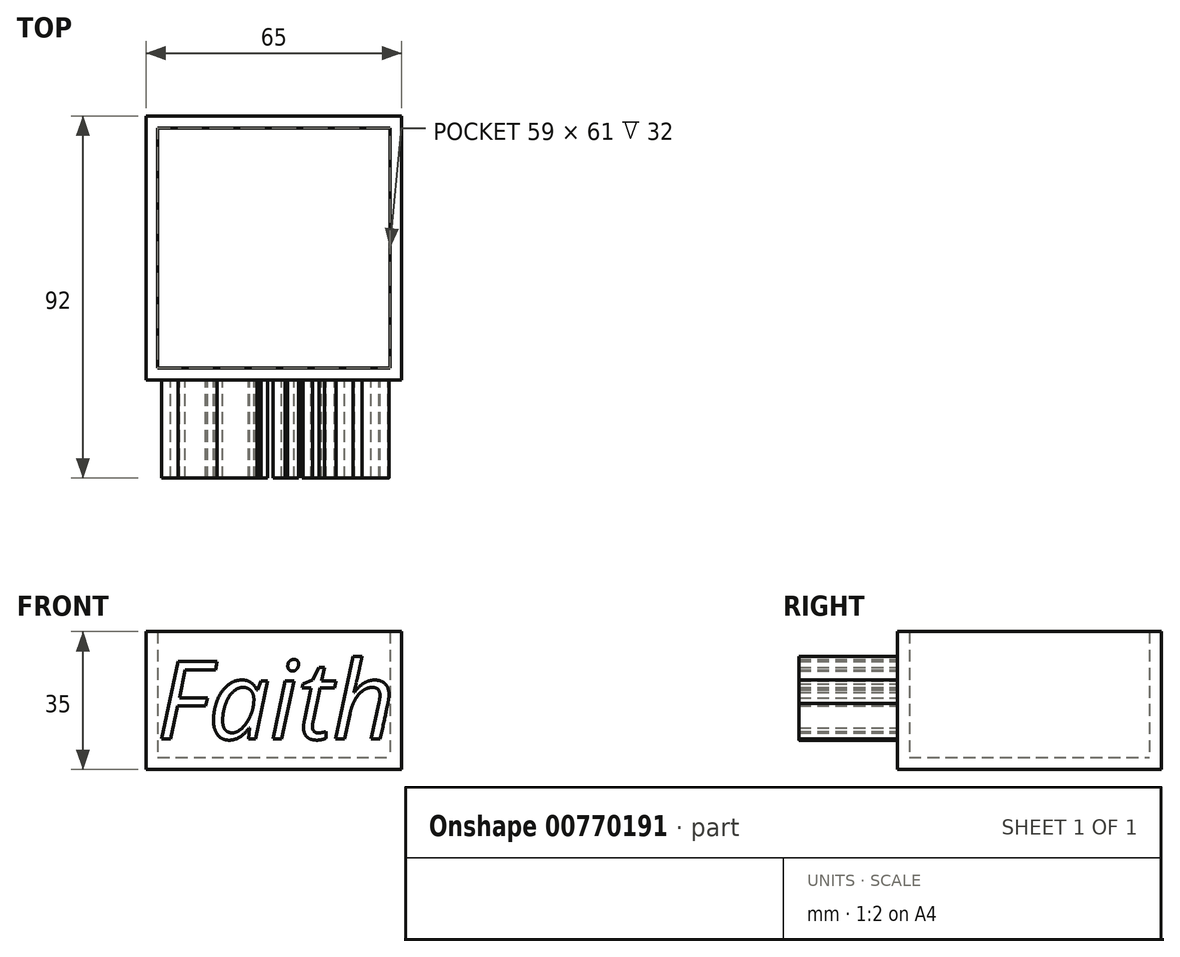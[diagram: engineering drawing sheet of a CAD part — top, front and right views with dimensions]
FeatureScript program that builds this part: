
annotation { "Feature Type Name" : "Feature", "Feature Type Description" : "" }
export const myFeature = defineFeature(function(context is Context, id is Id, definition is map)
    precondition{}
    {
        {
            var Q0;
            Q0=qCreatedBy(makeId("Front.planeOp"),FACE);
            var sketch = newSketch(context, id + "F0", { "sketchPlane" : qUnion([Q0])});
            skLineSegment(sketch, "E0.bottom", {"start": v(-49.28, 29.63) * mm, "end": v(15.72, 29.63) * mm});
            skLineSegment(sketch, "E0.top", {"start": v(-49.28, -5.37) * mm, "end": v(15.72, -5.37) * mm});
            skLineSegment(sketch, "E0.left", {"start": v(-49.28, 29.63) * mm, "end": v(-49.28, -5.37) * mm});
            skLineSegment(sketch, "E0.right", {"start": v(15.72, 29.63) * mm, "end": v(15.72, -5.37) * mm});
            skSolve(sketch);
        }
        {
            var Q0;
            Q0=makeQuery(id+"F0.imprint","IMPRINT",FACE,{"disambiguationData":[TD([[makeQuery(id+"F0.imprint","IMPRINT",EDGE,{"derivedFrom":sQuery(id+"F0.wireOp",EDGE,"E0.bottom")}),-1.0]])]});
            extrude(context, id + "F1", {"entities" : qUnion([Q0]), "depth" : 67 * mm, "offsetDistance" : 25 * mm});
        }
        {
            var Q0;
            Q0=makeQuery(id+"F1.opExtrude","SWEPT_FACE",FACE,{"disambiguationData":[OSD([sQuery(id+"F0.wireOp",EDGE,"E0.bottom")])]});
            shell(context, id + "F2", {"entities" : qUnion([Q0]), "thickness" : 3 * mm});
        }
        {
            var Q0;
            Q0=makeQuery(id+"F1.opExtrude","CAP_FACE",FACE,{"disambiguationData":[OSD([sQuery(id+"F0.wireOp",EDGE,"E0.bottom"),sQuery(id+"F0.wireOp",EDGE,"E0.top"),sQuery(id+"F0.wireOp",EDGE,"E0.left"),sQuery(id+"F0.wireOp",EDGE,"E0.right")])],"isStart":false});
            var sketch = newSketch(context, id + "F3", { "sketchPlane" : qUnion([Q0])});
            skText(sketch, "E1", { "text": "Faith", "fontName": "OpenSans-Italic.ttf"});
            const initialGuessF3  = {"E1": [-0.04644, 0.00233, 1, 0, 0.01987]};
            skSetInitialGuess(sketch, initialGuessF3);
            skSolve(sketch);
        }
        {
            var Q0;
            Q0 = qSketchRegion(id + "F3", true);
            extrude(context, id + "F4", {"entities" : qUnion([Q0]), "operationType" : NewBodyOperationType.ADD, "depth" : 25 * mm, "offsetDistance" : 25 * mm});
        }
    });
